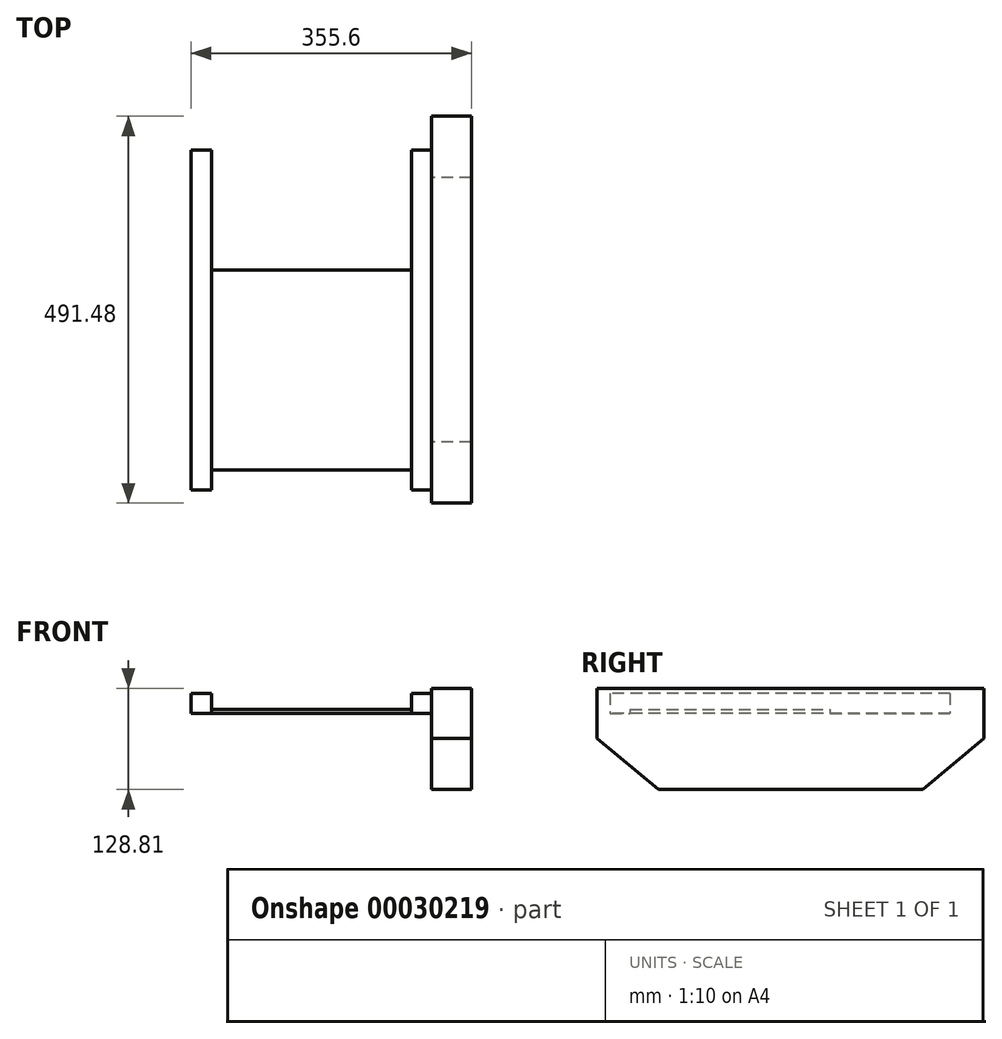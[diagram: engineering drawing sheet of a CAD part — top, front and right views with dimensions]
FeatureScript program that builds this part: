
annotation { "Feature Type Name" : "Feature", "Feature Type Description" : "" }
export const myFeature = defineFeature(function(context is Context, id is Id, definition is map)
    precondition{}
    {
        {
            var Q0;
            Q0=qCreatedBy(makeId("Top.planeOp"),FACE);
            var sketch = newSketch(context, id + "F0", { "sketchPlane" : qUnion([Q0])});
            skLineSegment(sketch, "E0.rect.bottom", {"start": v(-127, -127) * mm, "end": v(127, -127) * mm});
            skLineSegment(sketch, "E0.rect.top", {"start": v(-127, 127) * mm, "end": v(127, 127) * mm});
            skLineSegment(sketch, "E0.rect.left", {"start": v(-127, -127) * mm, "end": v(-127, 127) * mm});
            skLineSegment(sketch, "E0.rect.right", {"start": v(127, -127) * mm, "end": v(127, 127) * mm});
            skPoint(sketch, "E0.rect.middle", {"position": v(0, 0) * mm});
            skLineSegment(sketch, "E1.top", {"start": v(-127, 279.4) * mm, "end": v(-152.4, 279.4) * mm});
            skLineSegment(sketch, "E1.left", {"start": v(-127, -127) * mm, "end": v(-127, 279.4) * mm});
            skLineSegment(sketch, "E1.right", {"start": v(-152.4, -127) * mm, "end": v(-152.4, 279.4) * mm});
            skLineSegment(sketch, "E2.bottom", {"start": v(-127, -127) * mm, "end": v(-127, -127) * mm});
            skLineSegment(sketch, "E2.top", {"start": v(-152.4, -152.4) * mm, "end": v(-127, -152.4) * mm});
            skLineSegment(sketch, "E2.left", {"start": v(-152.4, -127) * mm, "end": v(-152.4, -152.4) * mm});
            skLineSegment(sketch, "E2.right", {"start": v(-127, -127) * mm, "end": v(-127, -152.4) * mm});
            skLineSegment(sketch, "E3.top", {"start": v(127, -152.4) * mm, "end": v(152.4, -152.4) * mm});
            skLineSegment(sketch, "E3.left", {"start": v(127, -127) * mm, "end": v(127, -152.4) * mm});
            skLineSegment(sketch, "E3.right", {"start": v(152.4, -127) * mm, "end": v(152.4, -152.4) * mm});
            skLineSegment(sketch, "E4.top", {"start": v(127, 279.4) * mm, "end": v(152.4, 279.4) * mm});
            skLineSegment(sketch, "E4.left", {"start": v(127, -127) * mm, "end": v(127, 279.4) * mm});
            skLineSegment(sketch, "E4.right", {"start": v(152.4, -127) * mm, "end": v(152.4, 279.4) * mm});
            skLineSegment(sketch, "E5", {"start": v(0, 0) * mm, "end": v(0, 228.55) * mm});
            skSolve(sketch);
        }
        {
            var Q0;
            {var subQ2=sQuery(id+"F0.wireOp",EDGE,"E0.rect.bottom");Q0=makeQuery(id+"F0.imprint","IMPRINT",FACE,{"disambiguationData":[TD([[makeQuery(id+"F0.imprint","IMPRINT",EDGE,{"derivedFrom":subQ2}),1.0]])]});}
            extrude(context, id + "F1", {"entities" : qUnion([Q0]), "depth" : 5.08 * mm});
        }
        {
            var Q0;
            {var subQ2=sQuery(id+"F0.wireOp",EDGE,"E1.top");Q0=makeQuery(id+"F0.imprint","IMPRINT",FACE,{"disambiguationData":[TD([[makeQuery(id+"F0.imprint","IMPRINT",EDGE,{"derivedFrom":subQ2}),1.0]])]});}
            var Q1;
            Q1=makeQuery(id+"F0.imprint","IMPRINT",FACE,{"disambiguationData":[TD([[makeQuery(id+"F0.imprint","IMPRINT",EDGE,{"derivedFrom":sQuery(id+"F0.wireOp",EDGE,"E3.top")}),1.0]])]});
            extrude(context, id + "F2", {"entities" : qUnion([Q0, Q1]), "operationType" : NewBodyOperationType.ADD, "depth" : 25.4 * mm});
        }
        {
            var Q0;
            Q0=makeQuery(id+"F2.opExtrude","SWEPT_FACE",FACE,{"disambiguationData":[OSD([sQuery(id+"F0.wireOp",EDGE,"E3.right"),sQuery(id+"F0.wireOp",EDGE,"E4.right")])]});
            var sketch = newSketch(context, id + "F3", { "sketchPlane" : qUnion([Q0])});
            skLineSegment(sketch, "E6.rect.top", {"start": v(-168.9, 31.75) * mm, "end": v(168.9, 31.75) * mm});
            skLineSegment(sketch, "E6.rect.left", {"start": v(-168.9, -31.75) * mm, "end": v(-168.9, 31.75) * mm});
            skPoint(sketch, "E6.rect.middle", {"position": v(0, 0) * mm});
            skLineSegment(sketch, "E7.bottom", {"start": v(168.9, 31.75) * mm, "end": v(322.58, 31.75) * mm});
            skLineSegment(sketch, "E7.right", {"start": v(322.58, 31.75) * mm, "end": v(322.58, -31.75) * mm});
            skLineSegment(sketch, "E8", {"start": v(-168.9, -31.75) * mm, "end": v(-91.07, -97.06) * mm});
            skLineSegment(sketch, "E9", {"start": v(322.58, -31.75) * mm, "end": v(244.75, -97.06) * mm});
            skLineSegment(sketch, "E10", {"start": v(-91.07, -97.06) * mm, "end": v(244.75, -97.06) * mm});
            skPoint(sketch, "E6.rect.bottom.end.orphan", {"position": v(168.9, -31.75) * mm});
            skPoint(sketch, "E7.top.start.orphan", {"position": v(193.9, -31.75) * mm});
            skSolve(sketch);
        }
        {
            var Q0;
            Q0 = qSketchRegion(id + "F3", true);
            extrude(context, id + "F4", {"entities" : qUnion([Q0]), "operationType" : NewBodyOperationType.ADD, "depth" : 50.8 * mm});
        }
    });
